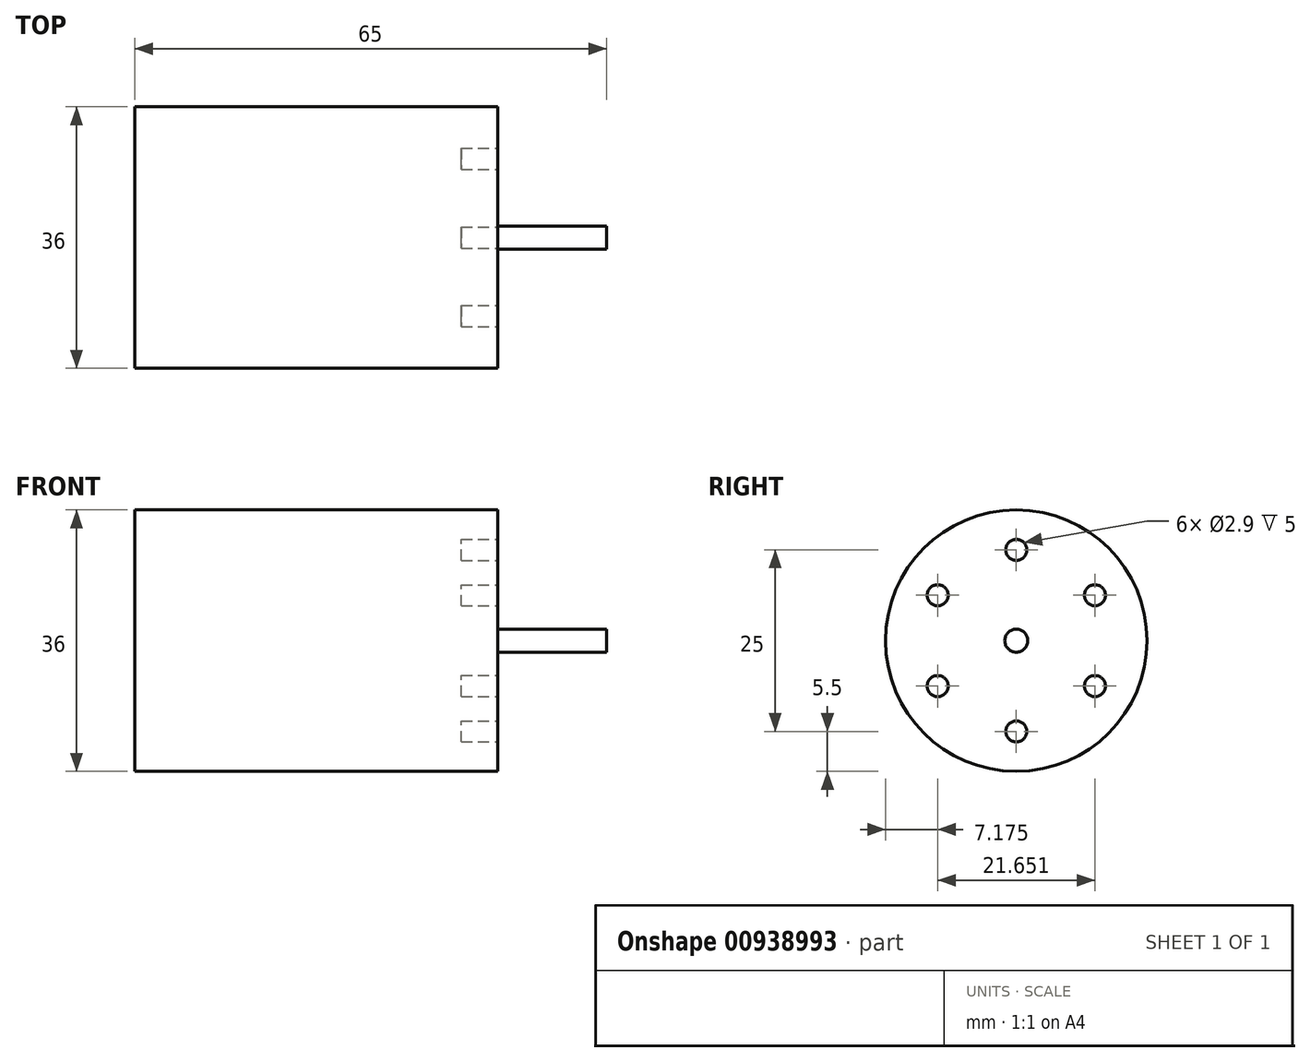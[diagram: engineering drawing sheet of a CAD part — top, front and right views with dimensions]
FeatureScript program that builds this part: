
annotation { "Feature Type Name" : "Feature", "Feature Type Description" : "" }
export const myFeature = defineFeature(function(context is Context, id is Id, definition is map)
    precondition{}
    {
        {
            var Q0;
            Q0=qCreatedBy(makeId("Right.planeOp"),FACE);
            var sketch = newSketch(context, id + "F0", { "sketchPlane" : qUnion([Q0])});
            skCircle(sketch, "E0", {"center": v(0, 0) * mm, "radius": 18 * mm});
            skSolve(sketch);
        }
        {
            var Q0;
            Q0=makeQuery(id+"F0.imprint","IMPRINT",FACE,{"disambiguationData":[TD([[makeQuery(id+"F0.imprint","IMPRINT",EDGE,{"derivedFrom":sQuery(id+"F0.wireOp",EDGE,"E0")}),1.0]])]});
            extrude(context, id + "F1", {"entities" : qUnion([Q0]), "depth" : 50 * mm, "offsetDistance" : 25 * mm, "symmetric" : true});
        }
        {
            var Q0;
            Q0=makeQuery(id+"F1.opExtrude","CAP_FACE",FACE,{"disambiguationData":[OSD([sQuery(id+"F0.wireOp",EDGE,"E0")])],"isStart":false});
            var sketch = newSketch(context, id + "F2", { "sketchPlane" : qUnion([Q0])});
            skCircle(sketch, "E1", {"center": v(0, 0) * mm, "radius": 1.59 * mm});
            skSolve(sketch);
        }
        {
            var Q0;
            Q0=makeQuery(id+"F2.imprint","IMPRINT",FACE,{"disambiguationData":[TD([[makeQuery(id+"F2.imprint","IMPRINT",EDGE,{"derivedFrom":sQuery(id+"F2.wireOp",EDGE,"E1")}),1.0]])]});
            extrude(context, id + "F3", {"entities" : qUnion([Q0]), "depth" : 15 * mm, "offsetDistance" : 25 * mm});
        }
        {
            var Q0;
            Q0=makeQuery(id+"F1.opExtrude","CAP_FACE",FACE,{"disambiguationData":[OSD([sQuery(id+"F0.wireOp",EDGE,"E0")])],"isStart":false});
            var sketch = newSketch(context, id + "F4", { "sketchPlane" : qUnion([Q0])});
            skCircle(sketch, "E2", {"center": v(0, 0) * mm, "radius": 12.5 * mm, "construction": true});
            skPoint(sketch, "E3", {"position": v(0, -12.5) * mm});
            skCircle(sketch, "E4", {"center": v(0, -12.5) * mm, "radius": 1.45 * mm});
            skCircle(sketch, "E5.1.0", {"center": v(10.83, -6.25) * mm, "radius": 1.45 * mm});
            skCircle(sketch, "E5.2.0", {"center": v(10.83, 6.25) * mm, "radius": 1.45 * mm});
            skCircle(sketch, "E5.3.0", {"center": v(0, 12.5) * mm, "radius": 1.45 * mm});
            skCircle(sketch, "E5.4.0", {"center": v(-10.83, 6.25) * mm, "radius": 1.45 * mm});
            skCircle(sketch, "E5.5.0", {"center": v(-10.83, -6.25) * mm, "radius": 1.45 * mm});
            skSolve(sketch);
        }
        {
            var Q0;
            Q0=makeQuery(id+"F4.imprint","IMPRINT",FACE,{"disambiguationData":[TD([[makeQuery(id+"F4.imprint","IMPRINT",EDGE,{"derivedFrom":sQuery(id+"F4.wireOp",EDGE,"E5.4.0")}),1.0]])]});
            var Q1;
            Q1=makeQuery(id+"F4.imprint","IMPRINT",FACE,{"disambiguationData":[TD([[makeQuery(id+"F4.imprint","IMPRINT",EDGE,{"derivedFrom":sQuery(id+"F4.wireOp",EDGE,"E5.3.0")}),1.0]])]});
            var Q2;
            Q2=makeQuery(id+"F4.imprint","IMPRINT",FACE,{"disambiguationData":[TD([[makeQuery(id+"F4.imprint","IMPRINT",EDGE,{"derivedFrom":sQuery(id+"F4.wireOp",EDGE,"E5.2.0")}),1.0]])]});
            var Q3;
            Q3=makeQuery(id+"F4.imprint","IMPRINT",FACE,{"disambiguationData":[TD([[makeQuery(id+"F4.imprint","IMPRINT",EDGE,{"derivedFrom":sQuery(id+"F4.wireOp",EDGE,"E5.1.0")}),1.0]])]});
            var Q4;
            Q4=makeQuery(id+"F4.imprint","IMPRINT",FACE,{"disambiguationData":[TD([[makeQuery(id+"F4.imprint","IMPRINT",EDGE,{"derivedFrom":sQuery(id+"F4.wireOp",EDGE,"E4")}),1.0]])]});
            var Q5;
            Q5=makeQuery(id+"F4.imprint","IMPRINT",FACE,{"disambiguationData":[TD([[makeQuery(id+"F4.imprint","IMPRINT",EDGE,{"derivedFrom":sQuery(id+"F4.wireOp",EDGE,"E5.5.0")}),1.0]])]});
            extrude(context, id + "F5", {"entities" : qUnion([Q0, Q1, Q2, Q3, Q4, Q5]), "operationType" : NewBodyOperationType.REMOVE, "oppositeDirection" : true, "depth" : 5 * mm, "offsetDistance" : 25 * mm});
        }
    });
